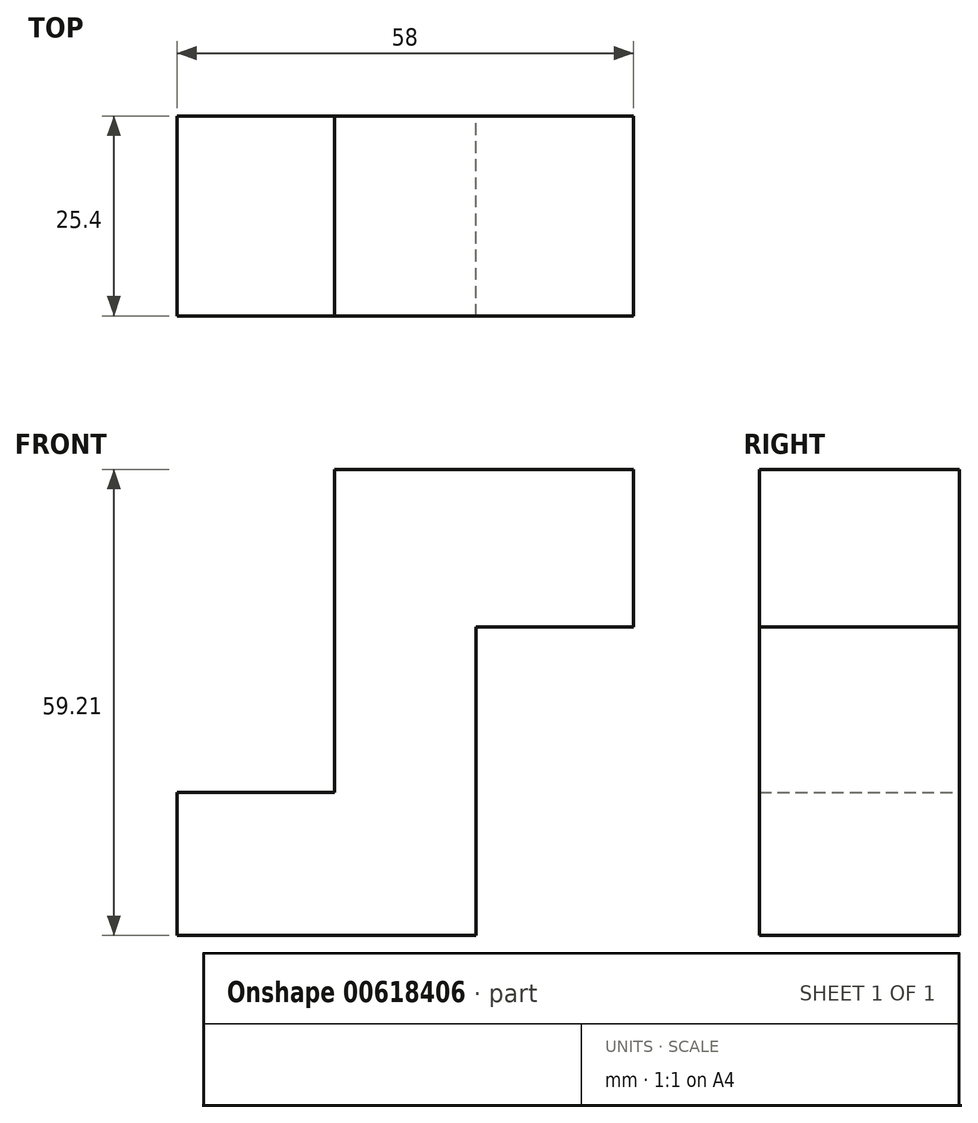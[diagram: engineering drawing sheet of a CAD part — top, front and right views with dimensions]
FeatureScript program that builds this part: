
annotation { "Feature Type Name" : "Feature", "Feature Type Description" : "" }
export const myFeature = defineFeature(function(context is Context, id is Id, definition is map)
    precondition{}
    {
        {
            var Q0;
            Q0=qCreatedBy(makeId("Front.planeOp"),FACE);
            var sketch = newSketch(context, id + "F0", { "sketchPlane" : qUnion([Q0])});
            skLineSegment(sketch, "E0", {"start": v(-38, -21) * mm, "end": v(-38, -39.2) * mm});
            skLineSegment(sketch, "E1", {"start": v(-38, -39.2) * mm, "end": v(0, -39.2) * mm});
            skLineSegment(sketch, "E2", {"start": v(0, -39.2) * mm, "end": v(0, 0) * mm});
            skLineSegment(sketch, "E3", {"start": v(-38, -21) * mm, "end": v(-18, -21) * mm});
            skLineSegment(sketch, "E4", {"start": v(-18, -21) * mm, "end": v(-18, 20) * mm});
            skLineSegment(sketch, "E5", {"start": v(-18, 20) * mm, "end": v(20, 20) * mm});
            skLineSegment(sketch, "E6", {"start": v(20, 20) * mm, "end": v(20, 0) * mm});
            skLineSegment(sketch, "E7", {"start": v(20, 0) * mm, "end": v(0, 0) * mm});
            skSolve(sketch);
        }
        {
            var Q0;
            Q0 = qSketchRegion(id + "F0", true);
            extrude(context, id + "F1", {"entities" : qUnion([Q0]), "depth" : 25.4 * mm, "offsetDistance" : 25.4 * mm});
        }
    });
